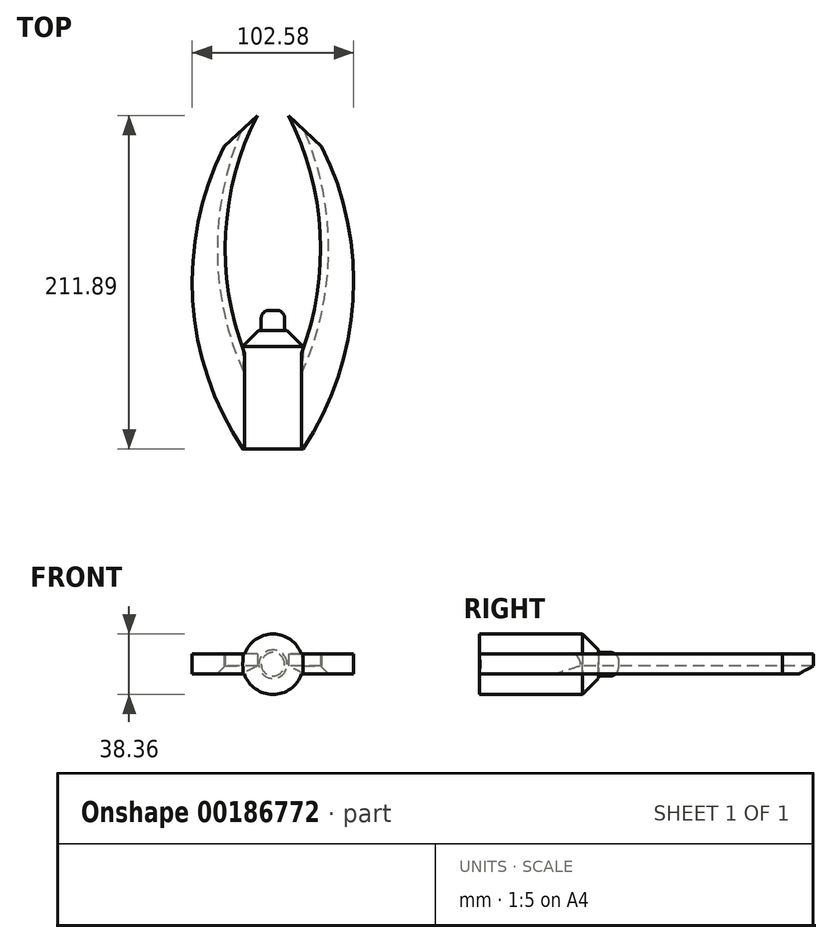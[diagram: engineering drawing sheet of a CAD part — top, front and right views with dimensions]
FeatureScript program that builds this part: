
annotation { "Feature Type Name" : "Feature", "Feature Type Description" : "" }
export const myFeature = defineFeature(function(context is Context, id is Id, definition is map)
    precondition{}
    {
        {
            var Q0;
            Q0=qCreatedBy(makeId("Top.planeOp"),FACE);
            var sketch = newSketch(context, id + "F0", { "sketchPlane" : qUnion([Q0])});
            skArc(sketch, "E0", {"start": v(-9.87, 186.49) * mm, "mid": v(-30.03, 91.92) * mm, "end": v(0, 0) * mm});
            skArc(sketch, "E1.MirrorCS", {"start": v(9.87, 186.49) * mm, "mid": v(30.03, 91.92) * mm, "end": v(0, 0) * mm});
            skArc(sketch, "E2", {"start": v(-30.95, 166.75) * mm, "mid": v(-49.36, 53.87) * mm, "end": v(0, -49.31) * mm});
            skArc(sketch, "E3.MirrorCS", {"start": v(30.95, 166.75) * mm, "mid": v(49.36, 53.87) * mm, "end": v(0, -49.31) * mm});
            skLineSegment(sketch, "E4", {"start": v(-9.87, 186.49) * mm, "end": v(-30.95, 166.75) * mm});
            skLineSegment(sketch, "E5", {"start": v(9.87, 186.49) * mm, "end": v(30.95, 166.75) * mm});
            skSolve(sketch);
        }
        {
            var Q0;
            Q0 = qSketchRegion(id + "F0", true);
            extrude(context, id + "F1", {"entities" : qUnion([Q0]), "depth" : 12.7 * mm});
        }
        {
            var Q0;
            Q0=qCreatedBy(makeId("Front.planeOp"),FACE);
            var sketch = newSketch(context, id + "F2", { "sketchPlane" : qUnion([Q0])});
            skCircle(sketch, "E6", {"center": v(0, 6.25) * mm, "radius": 19.18 * mm});
            skSolve(sketch);
        }
        {
            var Q0;
            Q0 = qSketchRegion(id + "F2", true);
            extrude(context, id + "F3", {"entities" : qUnion([Q0]), "operationType" : NewBodyOperationType.ADD, "depth" : 25.4 * mm, "hasSecondDirection" : true, "secondDirectionOppositeDirection" : true, "secondDirectionDepth" : 50.04 * mm});
        }
        {
            var Q0;
            Q0=makeQuery(id+"F1.opExtrude","CAP_EDGE",EDGE,{"disambiguationData":[OSD([sQuery(id+"F0.wireOp",EDGE,"E1.MirrorCS")])],"isStart":true});
            chamfer(context, id + "F4", {"entities" : qUnion([Q0]), "width" : 5.08 * mm, "tangentPropagation" : true});
        }
        {
            var Q0;
            Q0=makeQuery(id+"F1.opExtrude","CAP_EDGE",EDGE,{"disambiguationData":[OSD([sQuery(id+"F0.wireOp",EDGE,"E0")])],"isStart":true});
            chamfer(context, id + "F5", {"entities" : qUnion([Q0]), "width" : 5.08 * mm, "tangentPropagation" : true});
        }
        {
            var Q0;
            Q0=makeQuery(id+"F1.opExtrude","CAP_FACE",FACE,{"disambiguationData":[OSD([sQuery(id+"F0.wireOp",EDGE,"E0"),sQuery(id+"F0.wireOp",EDGE,"E1.MirrorCS"),sQuery(id+"F0.wireOp",EDGE,"E2"),sQuery(id+"F0.wireOp",EDGE,"E3.MirrorCS"),sQuery(id+"F0.wireOp",EDGE,"E4"),sQuery(id+"F0.wireOp",EDGE,"E5")])],"isStart":true});
            var sketch = newSketch(context, id + "F6", { "sketchPlane" : qUnion([Q0])});
            skArc(sketch, "E7", {"start": v(0, 49.31) * mm, "mid": v(-10, 37.78) * mm, "end": v(-18.95, 25.4) * mm});
            skArc(sketch, "E8", {"start": v(18.95, 25.4) * mm, "mid": v(10.05, 37.81) * mm, "end": v(0, 49.31) * mm});
            skLineSegment(sketch, "E9", {"start": v(-18.95, 25.4) * mm, "end": v(18.95, 25.4) * mm});
            skSolve(sketch);
        }
        {
            var Q0;
            Q0=makeQuery(id+"F3.opExtrude","CAP_FACE",FACE,{"disambiguationData":[OSD([sQuery(id+"F2.wireOp",EDGE,"E6")])],"isStart":true});
            chamfer(context, id + "F7", {"entities" : qUnion([Q0]), "width" : 10.16 * mm, "tangentPropagation" : true});
        }
        {
            var Q0;
            Q0 = qSketchRegion(id + "F6", true);
            extrude(context, id + "F8", {"entities" : qUnion([Q0]), "operationType" : NewBodyOperationType.REMOVE, "oppositeDirection" : true, "depth" : 25.4 * mm});
        }
        {
            var Q0;
            Q0=makeQuery(id+"F3.opExtrude","CAP_FACE",FACE,{"disambiguationData":[OSD([sQuery(id+"F2.wireOp",EDGE,"E6")])],"isStart":true});
            var sketch = newSketch(context, id + "F9", { "sketchPlane" : qUnion([Q0])});
            skCircle(sketch, "E10", {"center": v(0, 6.25) * mm, "radius": 7.42 * mm});
            skSolve(sketch);
        }
        {
            var Q0;
            Q0 = qSketchRegion(id + "F9", true);
            extrude(context, id + "F10", {"entities" : qUnion([Q0]), "operationType" : NewBodyOperationType.ADD, "depth" : 12.7 * mm});
        }
        {
            var Q0;
            Q0=makeQuery(id+"F10.opExtrude","CAP_FACE",FACE,{"disambiguationData":[OSD([sQuery(id+"F9.wireOp",EDGE,"E10")])],"isStart":false});
            fillet(context, id + "F11", {"entities" : qUnion([Q0]), "radius" : 5.08 * mm, "tangentPropagation" : true, "allowEdgeOverflow" : false});
        }
    });
